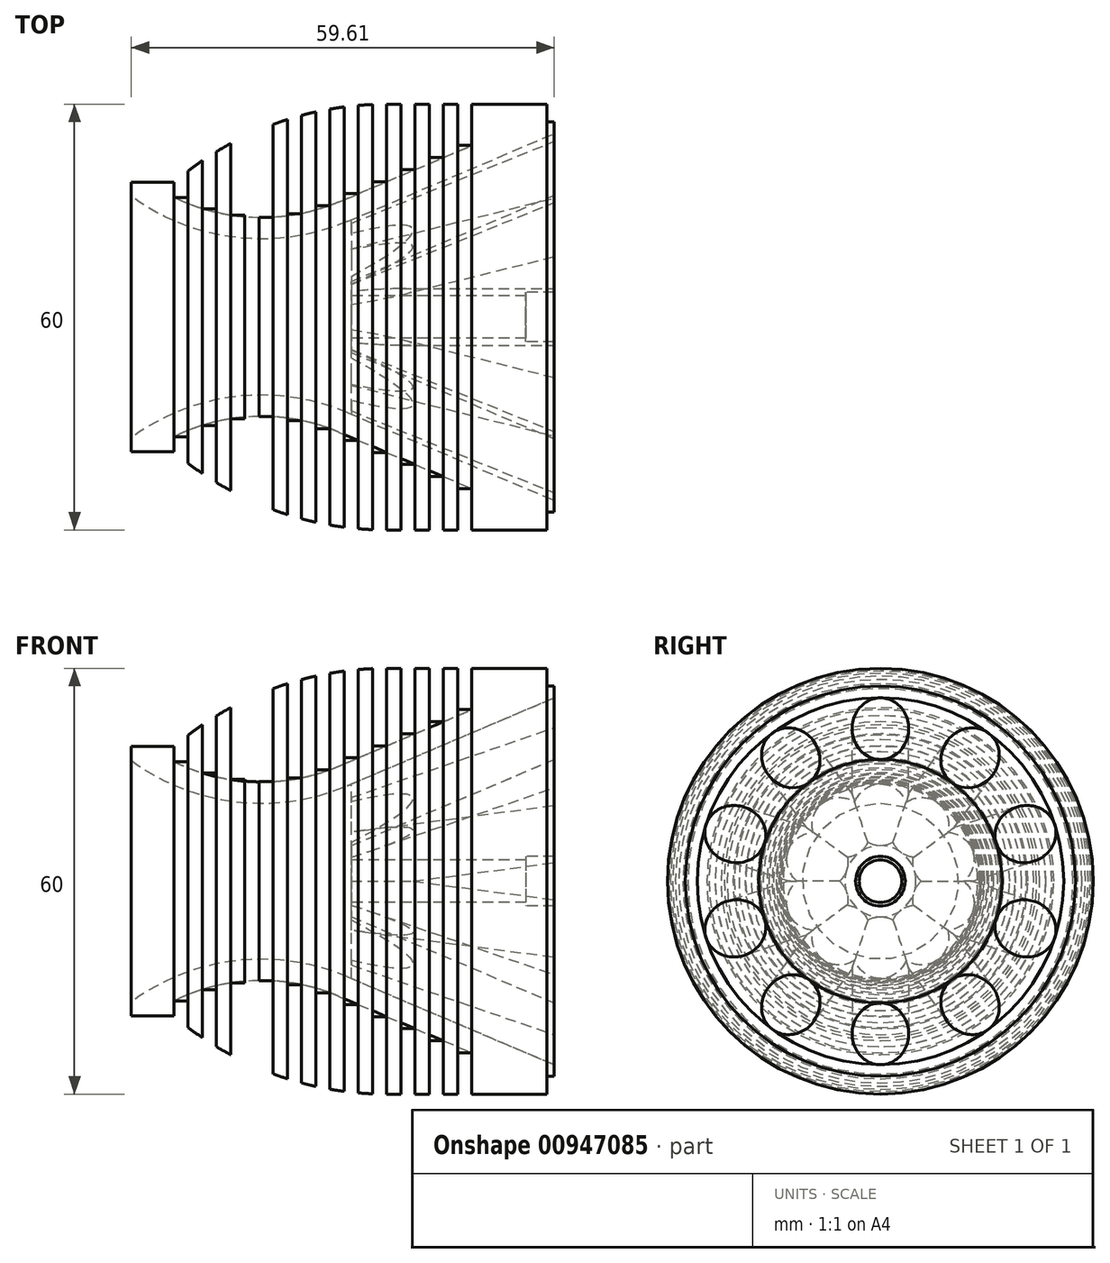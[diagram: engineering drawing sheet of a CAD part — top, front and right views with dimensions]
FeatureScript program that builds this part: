
annotation { "Feature Type Name" : "Feature", "Feature Type Description" : "" }
export const myFeature = defineFeature(function(context is Context, id is Id, definition is map)
    precondition{}
    {
        {
            var Q0;
            Q0=qCreatedBy(makeId("Front.planeOp"),FACE);
            var sketch = newSketch(context, id + "F0", { "sketchPlane" : qUnion([Q0])});
            skLineSegment(sketch, "E0", {"start": v(0, 0) * mm, "end": v(59.61, 0) * mm, "construction": true});
            skLineSegment(sketch, "E1", {"start": v(59.61, 27.5) * mm, "end": v(59.61, -27.5) * mm});
            skLineSegment(sketch, "E2", {"start": v(59.61, 27.5) * mm, "end": v(58.61, 27.5) * mm});
            skLineSegment(sketch, "E3", {"start": v(58.61, 27.5) * mm, "end": v(58.61, 30) * mm});
            skLineSegment(sketch, "E4.0.MirrorCS", {"start": v(58.61, -27.5) * mm, "end": v(58.61, -30) * mm});
            skLineSegment(sketch, "E5.0.MirrorCS", {"start": v(59.61, -27.5) * mm, "end": v(58.61, -27.5) * mm});
            skLineSegment(sketch, "E6", {"start": v(58.61, 30) * mm, "end": v(48, 30) * mm});
            skLineSegment(sketch, "E7.0.MirrorCS", {"start": v(58.61, -30) * mm, "end": v(48, -30) * mm});
            skLineSegment(sketch, "E8", {"start": v(0, 17) * mm, "end": v(0, -17) * mm});
            skLineSegment(sketch, "E9", {"start": v(59.61, 3.5) * mm, "end": v(55.61, 3.5) * mm});
            skLineSegment(sketch, "E10", {"start": v(55.61, 3.5) * mm, "end": v(55.61, 3) * mm});
            skLineSegment(sketch, "E11", {"start": v(55.61, 3) * mm, "end": v(31, 3) * mm});
            skLineSegment(sketch, "E12", {"start": v(31, 3) * mm, "end": v(31, 5) * mm});
            skLineSegment(sketch, "E13", {"start": v(31, 5) * mm, "end": v(59.61, 17.15) * mm});
            skLineSegment(sketch, "E14", {"start": v(59.61, 25.85) * mm, "end": v(30.44, 13.46) * mm});
            skLineSegment(sketch, "E15.0.MirrorCS", {"start": v(59.61, -3.5) * mm, "end": v(55.61, -3.5) * mm});
            skLineSegment(sketch, "E16.0.MirrorCS", {"start": v(55.61, -3.5) * mm, "end": v(55.61, -3) * mm});
            skLineSegment(sketch, "E17.0.MirrorCS", {"start": v(55.61, -3) * mm, "end": v(31, -3) * mm});
            skLineSegment(sketch, "E18.0.MirrorCS", {"start": v(31, -3) * mm, "end": v(31, -5) * mm});
            skLineSegment(sketch, "E19.0.MirrorCS", {"start": v(31, -5) * mm, "end": v(59.61, -17.15) * mm});
            skLineSegment(sketch, "E20.0.MirrorCS", {"start": v(59.61, -25.85) * mm, "end": v(30.44, -13.46) * mm});
            skArc(sketch, "E21", {"start": v(30.44, 13.46) * mm, "mid": v(14.75, 11.2) * mm, "end": v(0, 17) * mm});
            skArc(sketch, "E22.0.MirrorCS", {"start": v(30.44, -13.46) * mm, "mid": v(14.75, -11.2) * mm, "end": v(0, -17) * mm});
            skArc(sketch, "E23.0", {"start": v(29.27, 16.23) * mm, "mid": v(17.57, 14.01) * mm, "end": v(6, 16.86) * mm});
            skLineSegment(sketch, "E23.1", {"start": v(48, 24.18) * mm, "end": v(29.27, 16.23) * mm});
            skLineSegment(sketch, "E24", {"start": v(0, 17) * mm, "end": v(0, 19) * mm});
            skLineSegment(sketch, "E25.0.MirrorCS", {"start": v(48, -24.18) * mm, "end": v(29.27, -16.23) * mm});
            skArc(sketch, "E26.0.MirrorCS", {"start": v(29.27, -16.23) * mm, "mid": v(17.57, -14.01) * mm, "end": v(6, -16.86) * mm});
            skLineSegment(sketch, "E27.0.MirrorCS", {"start": v(0, -17) * mm, "end": v(0, -19) * mm});
            skLineSegment(sketch, "E28", {"start": v(48, 30) * mm, "end": v(48, 24.18) * mm});
            skLineSegment(sketch, "E29.0.MirrorCS", {"start": v(48, -30) * mm, "end": v(48, -24.18) * mm});
            skLineSegment(sketch, "E30", {"start": v(6, -19) * mm, "end": v(6, -16.86) * mm});
            skLineSegment(sketch, "E31.0.MirrorCS", {"start": v(6, 19) * mm, "end": v(6, 16.86) * mm});
            skLineSegment(sketch, "E32", {"start": v(0, 19) * mm, "end": v(6, 19) * mm});
            skLineSegment(sketch, "E33.0.MirrorCS", {"start": v(0, -19) * mm, "end": v(6, -19) * mm});
            skLineSegment(sketch, "E34", {"start": v(31, 5) * mm, "end": v(31, 13.7) * mm});
            skLineSegment(sketch, "E35.0.MirrorCS", {"start": v(31, -5) * mm, "end": v(31, -13.7) * mm});
            skPoint(sketch, "E36", {"position": v(31, 9.36) * mm});
            skLineSegment(sketch, "E37", {"start": v(25.3, 6.93) * mm, "end": v(66.16, 24.28) * mm, "construction": true});
            skPoint(sketch, "E38", {"position": v(59.61, 21.5) * mm});
            skPoint(sketch, "E39.0.MirrorP", {"position": v(59.61, -21.5) * mm});
            skSolve(sketch);
        }
        {
            var Q0;
            Q0=qCreatedBy(makeId("Front.planeOp"),FACE);
            var sketch = newSketch(context, id + "F1", { "sketchPlane" : qUnion([Q0])});
            skLineSegment(sketch, "E40.0", {"start": v(48, 30) * mm, "end": v(48, 24.18) * mm});
            skLineSegment(sketch, "E40.1", {"start": v(48, 24.18) * mm, "end": v(29.27, 16.23) * mm});
            skArc(sketch, "E40.2", {"start": v(29.27, 16.23) * mm, "mid": v(17.57, 14.01) * mm, "end": v(6, 16.86) * mm});
            skLineSegment(sketch, "E40.5", {"start": v(58.61, 30) * mm, "end": v(48, 30) * mm});
            skLineSegment(sketch, "E41", {"start": v(48, 30) * mm, "end": v(36, 30) * mm});
            skArc(sketch, "E42", {"start": v(36, 30) * mm, "mid": v(20.02, 27.16) * mm, "end": v(6, 19) * mm});
            skLineSegment(sketch, "E43", {"start": v(8, 15.98) * mm, "end": v(8, 20.6) * mm});
            skLineSegment(sketch, "E44", {"start": v(10, 15.27) * mm, "end": v(10, 22.03) * mm});
            skLineSegment(sketch, "E45", {"start": v(12, 14.72) * mm, "end": v(12, 23.31) * mm});
            skLineSegment(sketch, "E46", {"start": v(14, 14.34) * mm, "end": v(14, 24.45) * mm});
            skLineSegment(sketch, "E47", {"start": v(16, 14.1) * mm, "end": v(16, 25.47) * mm});
            skLineSegment(sketch, "E48", {"start": v(18, 14) * mm, "end": v(18, 26.37) * mm});
            skLineSegment(sketch, "E49", {"start": v(20, 14.05) * mm, "end": v(20, 27.15) * mm});
            skLineSegment(sketch, "E50", {"start": v(22, 14.24) * mm, "end": v(22, 27.84) * mm});
            skLineSegment(sketch, "E51", {"start": v(24, 14.58) * mm, "end": v(24, 28.42) * mm});
            skLineSegment(sketch, "E52", {"start": v(26, 15.07) * mm, "end": v(26, 28.9) * mm});
            skLineSegment(sketch, "E53", {"start": v(8, 20.6) * mm, "end": v(10, 20.6) * mm, "construction": true});
            skLineSegment(sketch, "E54", {"start": v(10, 22.03) * mm, "end": v(12, 22.03) * mm, "construction": true});
            skLineSegment(sketch, "E55", {"start": v(12, 23.31) * mm, "end": v(14, 23.31) * mm, "construction": true});
            skLineSegment(sketch, "E56", {"start": v(14, 24.45) * mm, "end": v(16, 24.45) * mm, "construction": true});
            skLineSegment(sketch, "E57", {"start": v(16, 25.47) * mm, "end": v(18, 25.47) * mm, "construction": true});
            skLineSegment(sketch, "E58", {"start": v(18, 26.37) * mm, "end": v(20, 26.37) * mm, "construction": true});
            skLineSegment(sketch, "E59", {"start": v(20, 27.15) * mm, "end": v(22, 27.15) * mm, "construction": true});
            skLineSegment(sketch, "E60", {"start": v(22, 27.84) * mm, "end": v(24, 27.84) * mm, "construction": true});
            skLineSegment(sketch, "E61", {"start": v(24, 28.42) * mm, "end": v(26, 28.42) * mm, "construction": true});
            skLineSegment(sketch, "E62", {"start": v(28, 29.3) * mm, "end": v(28, 15.72) * mm});
            skLineSegment(sketch, "E63", {"start": v(32, 29.83) * mm, "end": v(32, 17.38) * mm});
            skLineSegment(sketch, "E64", {"start": v(34, 29.96) * mm, "end": v(34, 18.23) * mm});
            skLineSegment(sketch, "E65", {"start": v(36, 30) * mm, "end": v(36, 19.08) * mm});
            skLineSegment(sketch, "E66", {"start": v(38, 30) * mm, "end": v(38, 19.93) * mm});
            skLineSegment(sketch, "E67", {"start": v(40, 30) * mm, "end": v(40, 20.78) * mm});
            skLineSegment(sketch, "E68", {"start": v(42, 30) * mm, "end": v(42, 21.63) * mm});
            skLineSegment(sketch, "E69", {"start": v(26, 22) * mm, "end": v(28, 22) * mm, "construction": true});
            skLineSegment(sketch, "E70", {"start": v(28, 22.51) * mm, "end": v(30, 22.51) * mm, "construction": true});
            skLineSegment(sketch, "E71", {"start": v(30, 23.07) * mm, "end": v(32, 23.07) * mm, "construction": true});
            skLineSegment(sketch, "E72", {"start": v(32, 23.6) * mm, "end": v(34, 23.6) * mm, "construction": true});
            skLineSegment(sketch, "E73", {"start": v(34, 24.1) * mm, "end": v(36, 24.1) * mm, "construction": true});
            skLineSegment(sketch, "E74", {"start": v(36, 24.54) * mm, "end": v(38, 24.54) * mm, "construction": true});
            skLineSegment(sketch, "E75", {"start": v(38, 24.97) * mm, "end": v(40, 24.97) * mm, "construction": true});
            skLineSegment(sketch, "E76", {"start": v(40, 25.4) * mm, "end": v(42, 25.4) * mm, "construction": true});
            skLineSegment(sketch, "E77", {"start": v(44, 22.48) * mm, "end": v(44, 30) * mm});
            skLineSegment(sketch, "E78", {"start": v(46, 23.33) * mm, "end": v(46, 30) * mm});
            skLineSegment(sketch, "E79", {"start": v(42, 25.81) * mm, "end": v(44, 25.81) * mm, "construction": true});
            skLineSegment(sketch, "E80", {"start": v(44, 26.24) * mm, "end": v(46, 26.24) * mm, "construction": true});
            skLineSegment(sketch, "E81.0", {"start": v(6, 19) * mm, "end": v(6, 16.86) * mm});
            skLineSegment(sketch, "E81.1", {"start": v(0, 19) * mm, "end": v(6, 19) * mm});
            skLineSegment(sketch, "E81.2", {"start": v(0, 17) * mm, "end": v(0, 19) * mm});
            skLineSegment(sketch, "E82", {"start": v(30, 29.61) * mm, "end": v(30, 16.54) * mm});
            skLineSegment(sketch, "E83", {"start": v(6, 16.86) * mm, "end": v(8, 16.86) * mm});
            skLineSegment(sketch, "E84", {"start": v(10, 15.27) * mm, "end": v(12, 15.27) * mm});
            skLineSegment(sketch, "E85", {"start": v(14, 14.34) * mm, "end": v(16, 14.34) * mm});
            skLineSegment(sketch, "E86", {"start": v(20, 14.05) * mm, "end": v(18, 14.05) * mm});
            skLineSegment(sketch, "E87", {"start": v(24, 14.58) * mm, "end": v(22, 14.58) * mm});
            skLineSegment(sketch, "E88", {"start": v(28, 15.72) * mm, "end": v(26, 15.72) * mm});
            skLineSegment(sketch, "E89", {"start": v(32, 17.38) * mm, "end": v(30, 17.38) * mm});
            skLineSegment(sketch, "E90", {"start": v(36, 19.08) * mm, "end": v(34, 19.08) * mm});
            skLineSegment(sketch, "E91", {"start": v(40, 20.78) * mm, "end": v(38, 20.78) * mm});
            skLineSegment(sketch, "E92", {"start": v(44, 22.48) * mm, "end": v(42, 22.48) * mm});
            skLineSegment(sketch, "E93", {"start": v(48, 24.18) * mm, "end": v(46, 24.18) * mm});
            skSolve(sketch);
        }
        {
            var Q0;
            {var subQ5=sQuery(id+"F0.wireOp",EDGE,"E2");Q0=makeQuery(id+"F0.imprint","IMPRINT",FACE,{"disambiguationData":[TD([[makeQuery(id+"F0.imprint","IMPRINT",EDGE,{"derivedFrom":subQ5}),1.0]])]});}
            var Q1;
            {var subQ1=sQuery(id+"F0.wireOp",EDGE,"E9");Q1=makeQuery(id+"F0.imprint","IMPRINT",FACE,{"disambiguationData":[TD([[makeQuery(id+"F0.imprint","IMPRINT",EDGE,{"derivedFrom":subQ1}),-1.0]])]});}
            var Q2;
            {var subQ1=sQuery(id+"F0.wireOp",EDGE,"E15.0.MirrorCS");Q2=makeQuery(id+"F0.imprint","IMPRINT",FACE,{"disambiguationData":[TD([[makeQuery(id+"F0.imprint","IMPRINT",EDGE,{"derivedFrom":subQ1}),1.0]])]});}
            var Q3;
            Q3=makeQuery(id+"F0.imprint","IMPRINT",FACE,{"disambiguationData":[TD([[makeQuery(id+"F0.imprint","IMPRINT",EDGE,{"derivedFrom":sQuery(id+"F0.wireOp",EDGE,"E4.0.MirrorCS")}),-1.0]])]});
            var Q4;
            {var subQ5=sQuery(id+"F0.wireOp",EDGE,"E2");Q4=makeQuery(id+"F0.imprint","IMPRINT",FACE,{"disambiguationData":[TD([[makeQuery(id+"F0.imprint","IMPRINT",EDGE,{"derivedFrom":subQ5}),1.0]])]});}
            var Q5;
            Q5=makeQuery(id+"F0.imprint","IMPRINT",FACE,{"disambiguationData":[TD([[makeQuery(id+"F0.imprint","IMPRINT",EDGE,{"derivedFrom":sQuery(id+"F0.wireOp",EDGE,"E4.0.MirrorCS")}),-1.0]])]});
            var Q6;
            {var subQ0=sQuery(id+"F1.wireOp",EDGE,"E44");Q6=makeQuery(id+"F1.imprint","IMPRINT",FACE,{"disambiguationData":[TD([[makeQuery(id+"F1.imprint","IMPRINT",EDGE,{"derivedFrom":subQ0}),1.0]])]});}
            var Q7;
            {var subQ0=sQuery(id+"F1.wireOp",EDGE,"E46");Q7=makeQuery(id+"F1.imprint","IMPRINT",FACE,{"disambiguationData":[TD([[makeQuery(id+"F1.imprint","IMPRINT",EDGE,{"derivedFrom":subQ0}),1.0]])]});}
            var Q8;
            {var subQ2=sQuery(id+"F1.wireOp",EDGE,"E40.2");var subQ4=sQuery(id+"F1.wireOp",EDGE,"E47");var subQ8=makeQuery(id+"F1.imprint","INTERSECT",VERTEX,{"derivedFrom":[subQ2,subQ4]});Q8=makeQuery(id+"F1.imprint","IMPRINT",FACE,{"disambiguationData":[TD([[makeQuery(id+"F1.imprint","IMPRINT",EDGE,{"disambiguationData":[TD([[subQ8,1.0]])],"derivedFrom":subQ2}),-1.0]])]});}
            var Q9;
            {var subQ6=sQuery(id+"F1.wireOp",EDGE,"E49");Q9=makeQuery(id+"F1.imprint","IMPRINT",FACE,{"disambiguationData":[TD([[makeQuery(id+"F1.imprint","IMPRINT",EDGE,{"derivedFrom":subQ6}),-1.0]])]});}
            var Q10;
            {var subQ6=sQuery(id+"F1.wireOp",EDGE,"E51");Q10=makeQuery(id+"F1.imprint","IMPRINT",FACE,{"disambiguationData":[TD([[makeQuery(id+"F1.imprint","IMPRINT",EDGE,{"derivedFrom":subQ6}),-1.0]])]});}
            var Q11;
            {var subQ6=sQuery(id+"F1.wireOp",EDGE,"E62");Q11=makeQuery(id+"F1.imprint","IMPRINT",FACE,{"disambiguationData":[TD([[makeQuery(id+"F1.imprint","IMPRINT",EDGE,{"derivedFrom":subQ6}),1.0]])]});}
            var Q12;
            {var subQ6=sQuery(id+"F1.wireOp",EDGE,"E63");Q12=makeQuery(id+"F1.imprint","IMPRINT",FACE,{"disambiguationData":[TD([[makeQuery(id+"F1.imprint","IMPRINT",EDGE,{"derivedFrom":subQ6}),1.0]])]});}
            var Q13;
            {var subQ6=sQuery(id+"F1.wireOp",EDGE,"E65");Q13=makeQuery(id+"F1.imprint","IMPRINT",FACE,{"disambiguationData":[TD([[makeQuery(id+"F1.imprint","IMPRINT",EDGE,{"derivedFrom":subQ6}),1.0]])]});}
            var Q14;
            {var subQ6=sQuery(id+"F1.wireOp",EDGE,"E67");Q14=makeQuery(id+"F1.imprint","IMPRINT",FACE,{"disambiguationData":[TD([[makeQuery(id+"F1.imprint","IMPRINT",EDGE,{"derivedFrom":subQ6}),1.0]])]});}
            var Q15;
            {var subQ4=sQuery(id+"F1.wireOp",EDGE,"E77");Q15=makeQuery(id+"F1.imprint","IMPRINT",FACE,{"disambiguationData":[TD([[makeQuery(id+"F1.imprint","IMPRINT",EDGE,{"derivedFrom":subQ4}),-1.0]])]});}
            var Q16;
            {var subQ4=sQuery(id+"F0.wireOp",EDGE,"E13");Q16=makeQuery(id+"F0.imprint","IMPRINT",FACE,{"disambiguationData":[TD([[makeQuery(id+"F0.imprint","IMPRINT",EDGE,{"derivedFrom":subQ4}),1.0]])]});}
            var Q17;
            {var subQ0=sQuery(id+"F1.wireOp",EDGE,"E83");Q17=makeQuery(id+"F1.imprint","IMPRINT",FACE,{"disambiguationData":[TD([[makeQuery(id+"F1.imprint","IMPRINT",EDGE,{"derivedFrom":subQ0}),-1.0]])]});}
            var Q18;
            {var subQ0=sQuery(id+"F1.wireOp",EDGE,"E84");Q18=makeQuery(id+"F1.imprint","IMPRINT",FACE,{"disambiguationData":[TD([[makeQuery(id+"F1.imprint","IMPRINT",EDGE,{"derivedFrom":subQ0}),-1.0]])]});}
            var Q19;
            {var subQ0=sQuery(id+"F1.wireOp",EDGE,"E85");Q19=makeQuery(id+"F1.imprint","IMPRINT",FACE,{"disambiguationData":[TD([[makeQuery(id+"F1.imprint","IMPRINT",EDGE,{"derivedFrom":subQ0}),-1.0]])]});}
            var Q20;
            {var subQ0=sQuery(id+"F1.wireOp",EDGE,"E86");Q20=makeQuery(id+"F1.imprint","IMPRINT",FACE,{"disambiguationData":[TD([[makeQuery(id+"F1.imprint","IMPRINT",EDGE,{"derivedFrom":subQ0}),1.0]])]});}
            var Q21;
            {var subQ0=sQuery(id+"F1.wireOp",EDGE,"E87");Q21=makeQuery(id+"F1.imprint","IMPRINT",FACE,{"disambiguationData":[TD([[makeQuery(id+"F1.imprint","IMPRINT",EDGE,{"derivedFrom":subQ0}),1.0]])]});}
            var Q22;
            {var subQ0=sQuery(id+"F1.wireOp",EDGE,"E88");Q22=makeQuery(id+"F1.imprint","IMPRINT",FACE,{"disambiguationData":[TD([[makeQuery(id+"F1.imprint","IMPRINT",EDGE,{"derivedFrom":subQ0}),1.0]])]});}
            var Q23;
            {var subQ0=sQuery(id+"F1.wireOp",EDGE,"E89");Q23=makeQuery(id+"F1.imprint","IMPRINT",FACE,{"disambiguationData":[TD([[makeQuery(id+"F1.imprint","IMPRINT",EDGE,{"derivedFrom":subQ0}),1.0]])]});}
            var Q24;
            {var subQ0=sQuery(id+"F1.wireOp",EDGE,"E90");Q24=makeQuery(id+"F1.imprint","IMPRINT",FACE,{"disambiguationData":[TD([[makeQuery(id+"F1.imprint","IMPRINT",EDGE,{"derivedFrom":subQ0}),1.0]])]});}
            var Q25;
            {var subQ0=sQuery(id+"F1.wireOp",EDGE,"E91");Q25=makeQuery(id+"F1.imprint","IMPRINT",FACE,{"disambiguationData":[TD([[makeQuery(id+"F1.imprint","IMPRINT",EDGE,{"derivedFrom":subQ0}),1.0]])]});}
            var Q26;
            {var subQ0=sQuery(id+"F1.wireOp",EDGE,"E92");Q26=makeQuery(id+"F1.imprint","IMPRINT",FACE,{"disambiguationData":[TD([[makeQuery(id+"F1.imprint","IMPRINT",EDGE,{"derivedFrom":subQ0}),1.0]])]});}
            var Q27;
            {var subQ0=sQuery(id+"F1.wireOp",EDGE,"E93");Q27=makeQuery(id+"F1.imprint","IMPRINT",FACE,{"disambiguationData":[TD([[makeQuery(id+"F1.imprint","IMPRINT",EDGE,{"derivedFrom":subQ0}),1.0]])]});}
            var Q28;
            Q28=sQuery(id+"F0.wireOp",EDGE,"E0");
            revolve(context, id + "F2", {"entities" : qUnion([Q0, Q1, Q2, Q3, Q4, Q5, Q6, Q7, Q8, Q9, Q10, Q11, Q12, Q13, Q14, Q15, Q16, Q17, Q18, Q19, Q20, Q21, Q22, Q23, Q24, Q25, Q26, Q27]), "axis" : qUnion([Q28]), "revolveType" : RevolveType.FULL});
        }
        {
            var Q0;
            Q0=sQuery(id+"F0.wireOp",EDGE,"E37");
            var Q1;
            Q1=sQuery(id+"F0.wireOp",VERTEX,"E37.end");
            cPlane(context, id + "F3", {"entities" : qUnion([Q0, Q1]), "cplaneType" : CPlaneType.LINE_POINT, "offset" : 150 * mm, "width" : 150 * mm, "height" : 150 * mm});
        }
        {
            var Q0;
            Q0=qCreatedBy(id+"F3.planeOp",FACE);
            var sketch = newSketch(context, id + "F4", { "sketchPlane" : qUnion([Q0])});
            skPoint(sketch, "E94.0", {"position": v(0, -3.5) * mm});
            skCircle(sketch, "E95", {"center": v(0, -3.5) * mm, "radius": 4 * mm});
            skSolve(sketch);
        }
        {
            var Q0;
            Q0=makeQuery(id+"F4.imprint","IMPRINT",FACE,{"disambiguationData":[TD([[makeQuery(id+"F4.imprint","IMPRINT",EDGE,{"derivedFrom":sQuery(id+"F4.wireOp",EDGE,"E95")}),1.0]])]});
            extrude(context, id + "F5", {"entities" : qUnion([Q0]), "operationType" : NewBodyOperationType.REMOVE, "oppositeDirection" : true, "depth" : 45 * mm});
        }
        {
            var Q0;
            Q0=makeQuery(id+"F5.boolean.opBoolean","COPY",FACE,{"derivedFrom":makeQuery(id+"F5.opExtrude","SWEPT_FACE",FACE,{"disambiguationData":[OSD([sQuery(id+"F4.wireOp",EDGE,"E95")])]})});
            var Q1;
            Q1=makeQuery(id+"F2.opRevolve","SWEPT_FACE",FACE,{"disambiguationData":[OSD([sQuery(id+"F0.wireOp",EDGE,"E11")])]});
            circularPattern(context, id + "F6", {"faces" : qUnion([Q0]), "axis" : qUnion([Q1]), "angle" : 36 * degree, "instanceCount" : 10, "patternType" : PatternType.FACE, "computeTransformsWithoutBuiltin" : true});
        }
    });
